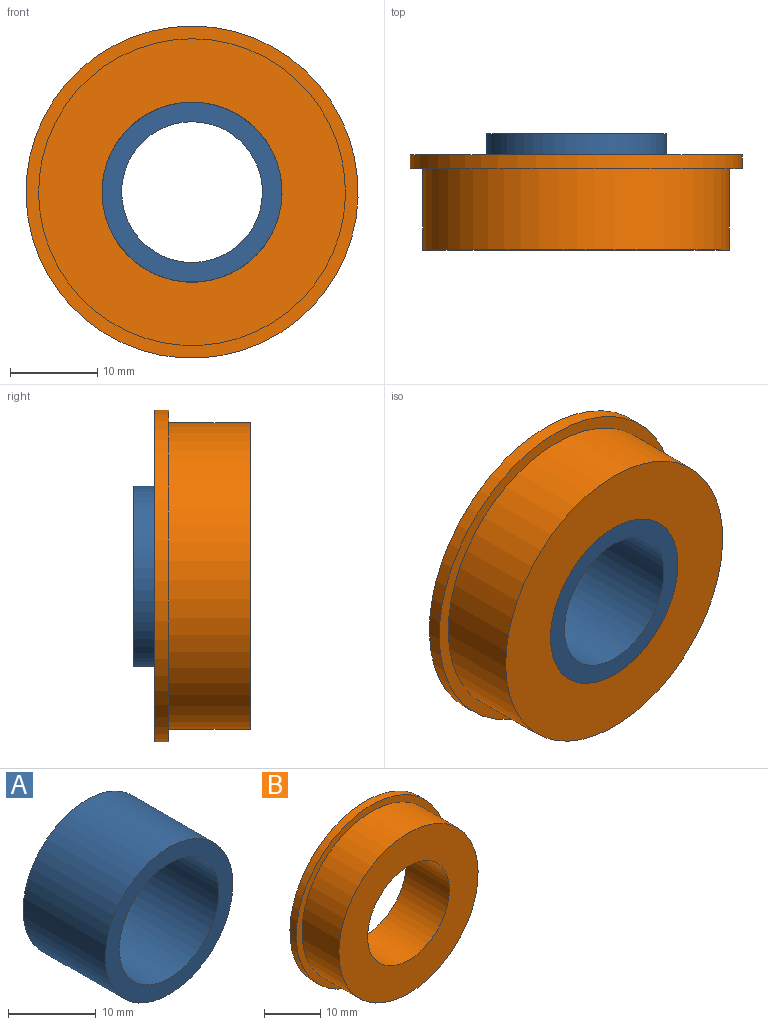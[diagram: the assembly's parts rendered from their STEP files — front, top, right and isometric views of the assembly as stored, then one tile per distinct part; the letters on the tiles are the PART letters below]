
ASSEMBLY  parts=2 mates=1
PART A: 4 faces, bbox 20.6x13.3x20.6 mm
  f0: cylinder r=8.05mm len=16.1mm, axis (0,1,0), area 672.7mm2, adj f2,f3
  f1: cylinder r=10.3mm len=20.6mm, axis (0,1,0), area 860.7mm2, adj f2,f3
  f2: plane 20.6x20.6mm, normal (0,-1,0), area 129.7mm2, adj f0,f1
  f3: plane 20.6x20.6mm, normal (0,1,0), area 129.7mm2, adj f0,f1
PART B: 6 faces, bbox 38x10.9x38 mm
  f0: cylinder r=10.3mm len=20.6mm, axis (0,1,0), area 705.4mm2, adj f2,f3
  f1: cylinder r=17.55mm len=35.1mm, axis (0,1,0), area 1025.5mm2, adj f2,f5
  f2: plane 35.1x35.1mm, normal (0,-1,0), area 634.3mm2, adj f0,f1
  f3: plane 38x38mm, normal (0,1,0), area 800.8mm2, adj f0,f4
  f4: cylinder r=19mm len=38mm, axis (0,1,0), area 191mm2, adj f3,f5
  f5: plane 38x38mm, normal (0,-1,0), area 166.5mm2, adj f1,f4
PLACE A rot(axis=(0,1,0),59.7deg) t=(31.65,0,-54.26)mm fixed
PLACE B rot(axis=(0,1,0),95.5deg) t=(-6.03,0,-62.53)mm
MATE revolute B.f0 <-> A.f0  axis (0,1,0) through (0,-10.9,0)mm
